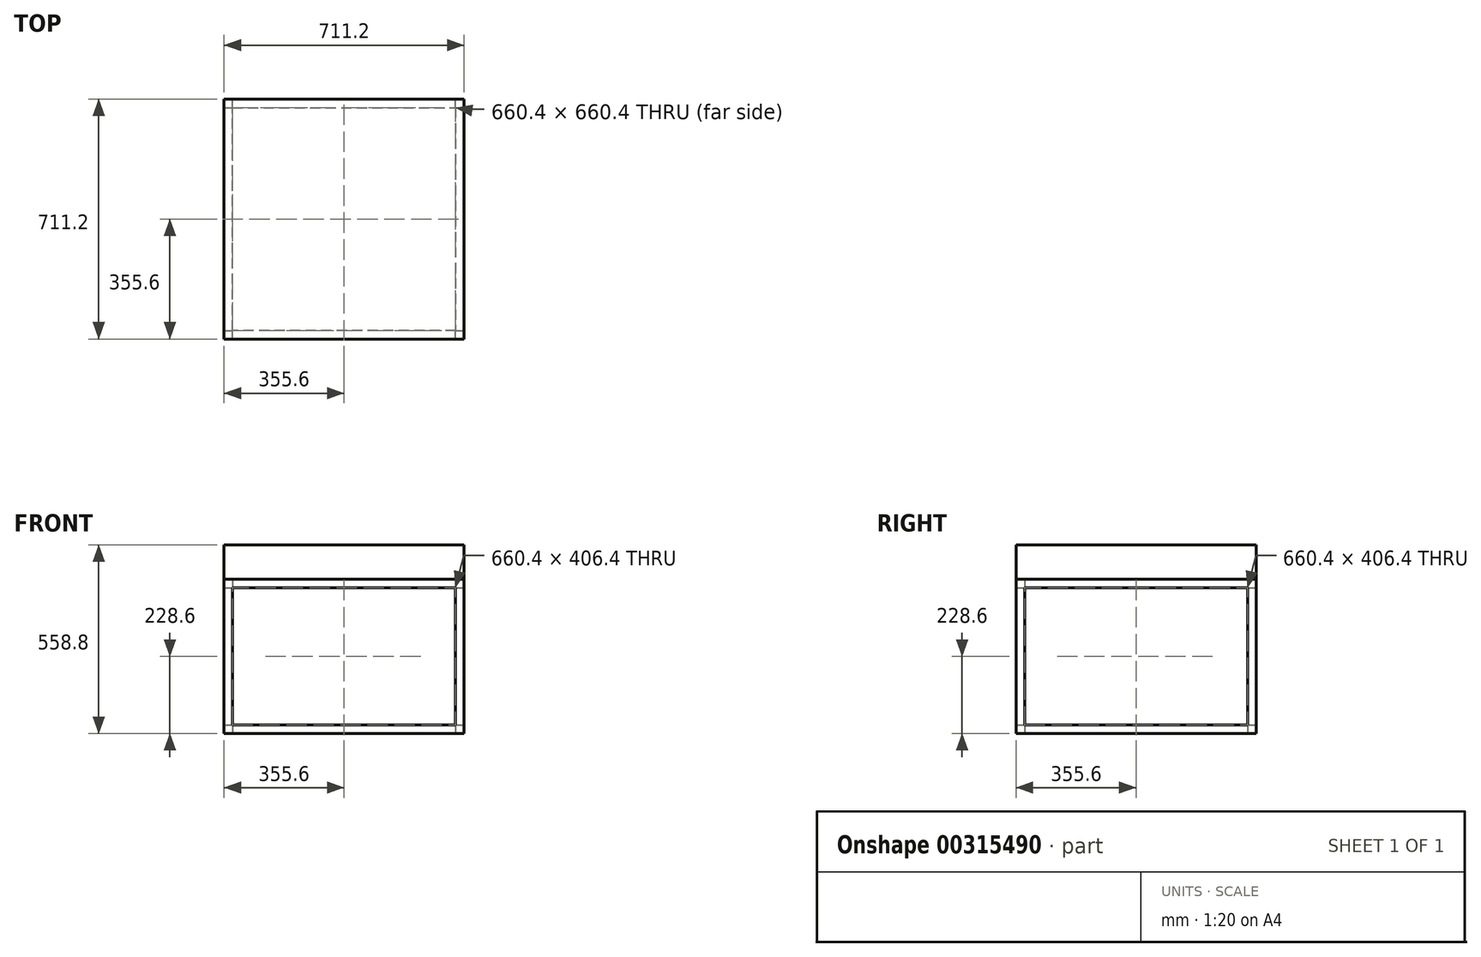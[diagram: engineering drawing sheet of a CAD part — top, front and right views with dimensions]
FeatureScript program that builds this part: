
annotation { "Feature Type Name" : "Feature", "Feature Type Description" : "" }
export const myFeature = defineFeature(function(context is Context, id is Id, definition is map)
    precondition{}
    {
        {
            var Q0;
            Q0=qCreatedBy(makeId("Front.planeOp"),FACE);
            var sketch = newSketch(context, id + "F0", { "sketchPlane" : qUnion([Q0])});
            skLineSegment(sketch, "E0.bottom", {"start": v(355.6, 228.6) * mm, "end": v(-355.6, 228.6) * mm});
            skLineSegment(sketch, "E0.top", {"start": v(355.6, -228.6) * mm, "end": v(-355.6, -228.6) * mm});
            skLineSegment(sketch, "E0.left", {"start": v(355.6, 228.6) * mm, "end": v(355.6, -228.6) * mm});
            skLineSegment(sketch, "E0.right", {"start": v(-355.6, 228.6) * mm, "end": v(-355.6, -228.6) * mm});
            skPoint(sketch, "E0.middle", {"position": v(0, 0) * mm});
            skLineSegment(sketch, "E1.0", {"start": v(-330.2, 203.2) * mm, "end": v(-330.2, -203.2) * mm});
            skLineSegment(sketch, "E1.1", {"start": v(330.2, 203.2) * mm, "end": v(-330.2, 203.2) * mm});
            skLineSegment(sketch, "E1.2", {"start": v(330.2, 203.2) * mm, "end": v(330.2, -203.2) * mm});
            skLineSegment(sketch, "E1.3", {"start": v(330.2, -203.2) * mm, "end": v(-330.2, -203.2) * mm});
            skSolve(sketch);
        }
        {
            var Q0;
            Q0=makeQuery(id+"F0.imprint","IMPRINT",FACE,{"disambiguationData":[TD([[makeQuery(id+"F0.imprint","IMPRINT",EDGE,{"derivedFrom":sQuery(id+"F0.wireOp",EDGE,"E0.bottom")}),1.0]])]});
            extrude(context, id + "F1", {"entities" : qUnion([Q0]), "depth" : 711.2 * mm});
        }
        {
            var Q0;
            Q0=makeQuery(id+"F1.opExtrude","SWEPT_FACE",FACE,{"disambiguationData":[OSD([sQuery(id+"F0.wireOp",EDGE,"E0.bottom")])]});
            var sketch = newSketch(context, id + "F2", { "sketchPlane" : qUnion([Q0])});
            skSolve(sketch);
        }
        {
            var Q0;
            Q0 = qSketchRegion(id + "F0", true);
            extrude(context, id + "F3", {"entities" : qUnion([Q0]), "depth" : 711.2 * mm});
        }
        {
            var Q0;
            Q0=makeQuery(id+"F3.opExtrude","SWEPT_FACE",FACE,{"disambiguationData":[OSD([sQuery(id+"F0.wireOp",EDGE,"E0.left")])]});
            var sketch = newSketch(context, id + "F4", { "sketchPlane" : qUnion([Q0])});
            skLineSegment(sketch, "E2.0", {"start": v(-25.4, -203.2) * mm, "end": v(-25.4, 203.2) * mm});
            skLineSegment(sketch, "E2.1", {"start": v(-685.8, -203.2) * mm, "end": v(-25.4, -203.2) * mm});
            skLineSegment(sketch, "E2.2", {"start": v(-685.8, 203.2) * mm, "end": v(-685.8, -203.2) * mm});
            skLineSegment(sketch, "E2.3", {"start": v(-25.4, 203.2) * mm, "end": v(-685.8, 203.2) * mm});
            skSolve(sketch);
        }
        {
            var Q0;
            Q0=makeQuery(id+"F4.imprint","IMPRINT",FACE,{"disambiguationData":[TD([[makeQuery(id+"F4.imprint","IMPRINT",EDGE,{"derivedFrom":sQuery(id+"F4.wireOp",EDGE,"E2.0")}),1.0]])]});
            extrude(context, id + "F5", {"entities" : qUnion([Q0]), "operationType" : NewBodyOperationType.REMOVE, "endBound" : BoundingType.THROUGH_ALL, "oppositeDirection" : true, "depth" : 25.4 * mm});
        }
        {
            var Q0;
            Q0=makeQuery(id+"F1.opExtrude","SWEPT_FACE",FACE,{"disambiguationData":[OSD([sQuery(id+"F0.wireOp",EDGE,"E0.top")])]});
            var sketch = newSketch(context, id + "F6", { "sketchPlane" : qUnion([Q0])});
            skLineSegment(sketch, "E3.0", {"start": v(-330.2, 25.4) * mm, "end": v(330.2, 25.4) * mm});
            skLineSegment(sketch, "E3.1", {"start": v(-330.2, 685.8) * mm, "end": v(-330.2, 25.4) * mm});
            skLineSegment(sketch, "E3.2", {"start": v(330.2, 685.8) * mm, "end": v(-330.2, 685.8) * mm});
            skLineSegment(sketch, "E3.3", {"start": v(330.2, 25.4) * mm, "end": v(330.2, 685.8) * mm});
            skSolve(sketch);
        }
        {
            var Q0;
            Q0 = qSketchRegion(id + "F6", true);
            var Q1;
            Q1=makeQuery(id+"F1.opExtrude","SWEPT_FACE",FACE,{"disambiguationData":[OSD([sQuery(id+"F0.wireOp",EDGE,"E0.bottom")])]});
            extrude(context, id + "F7", {"entities" : qUnion([Q0]), "operationType" : NewBodyOperationType.REMOVE, "endBound" : BoundingType.UP_TO_SURFACE, "oppositeDirection" : true, "endBoundEntityFace" : qUnion([Q1]), "depth" : 25.4 * mm});
        }
        {
            var Q0;
            {var subQ0=sQuery(id+"F0.wireOp",EDGE,"E0.bottom");Q0=makeQuery(id+"F2.imprint","IMPRINT",FACE,{"disambiguationData":[TD([[makeQuery(id+"F2.imprint","IMPRINT",EDGE,{"derivedFrom":makeQuery(id+"F1.opExtrude","CAP_EDGE",EDGE,{"disambiguationData":[OSD([subQ0])],"isStart":true})}),1.0]])]});}
            var sketch = newSketch(context, id + "F8", { "sketchPlane" : qUnion([Q0])});
            skLineSegment(sketch, "E4.0.0", {"start": v(355.6, -711.2) * mm, "end": v(355.6, 0) * mm});
            skLineSegment(sketch, "E4.0.1", {"start": v(355.6, 0) * mm, "end": v(-355.6, 0) * mm});
            skLineSegment(sketch, "E4.0.2", {"start": v(-355.6, 0) * mm, "end": v(-355.6, -711.2) * mm});
            skLineSegment(sketch, "E4.0.3", {"start": v(-355.6, -711.2) * mm, "end": v(355.6, -711.2) * mm});
            skSolve(sketch);
        }
        {
            var Q0;
            Q0 = qSketchRegion(id + "F8", true);
            extrude(context, id + "F9", {"entities" : qUnion([Q0]), "depth" : 101.6 * mm});
        }
        {
            var Q0;
            Q0=makeQuery(id+"F3.opExtrude","SWEPT_BODY",BODY,{"disambiguationData":[OSD([sQuery(id+"F0.wireOp",EDGE,"E0.bottom"),sQuery(id+"F0.wireOp",EDGE,"E0.top"),sQuery(id+"F0.wireOp",EDGE,"E0.left"),sQuery(id+"F0.wireOp",EDGE,"E0.right"),sQuery(id+"F0.wireOp",EDGE,"E1.0"),sQuery(id+"F0.wireOp",EDGE,"E1.1"),sQuery(id+"F0.wireOp",EDGE,"E1.2"),sQuery(id+"F0.wireOp",EDGE,"E1.3")])]});
            deleteBodies(context, id + "F10", {"entities" : qUnion([Q0])});
        }
    });
